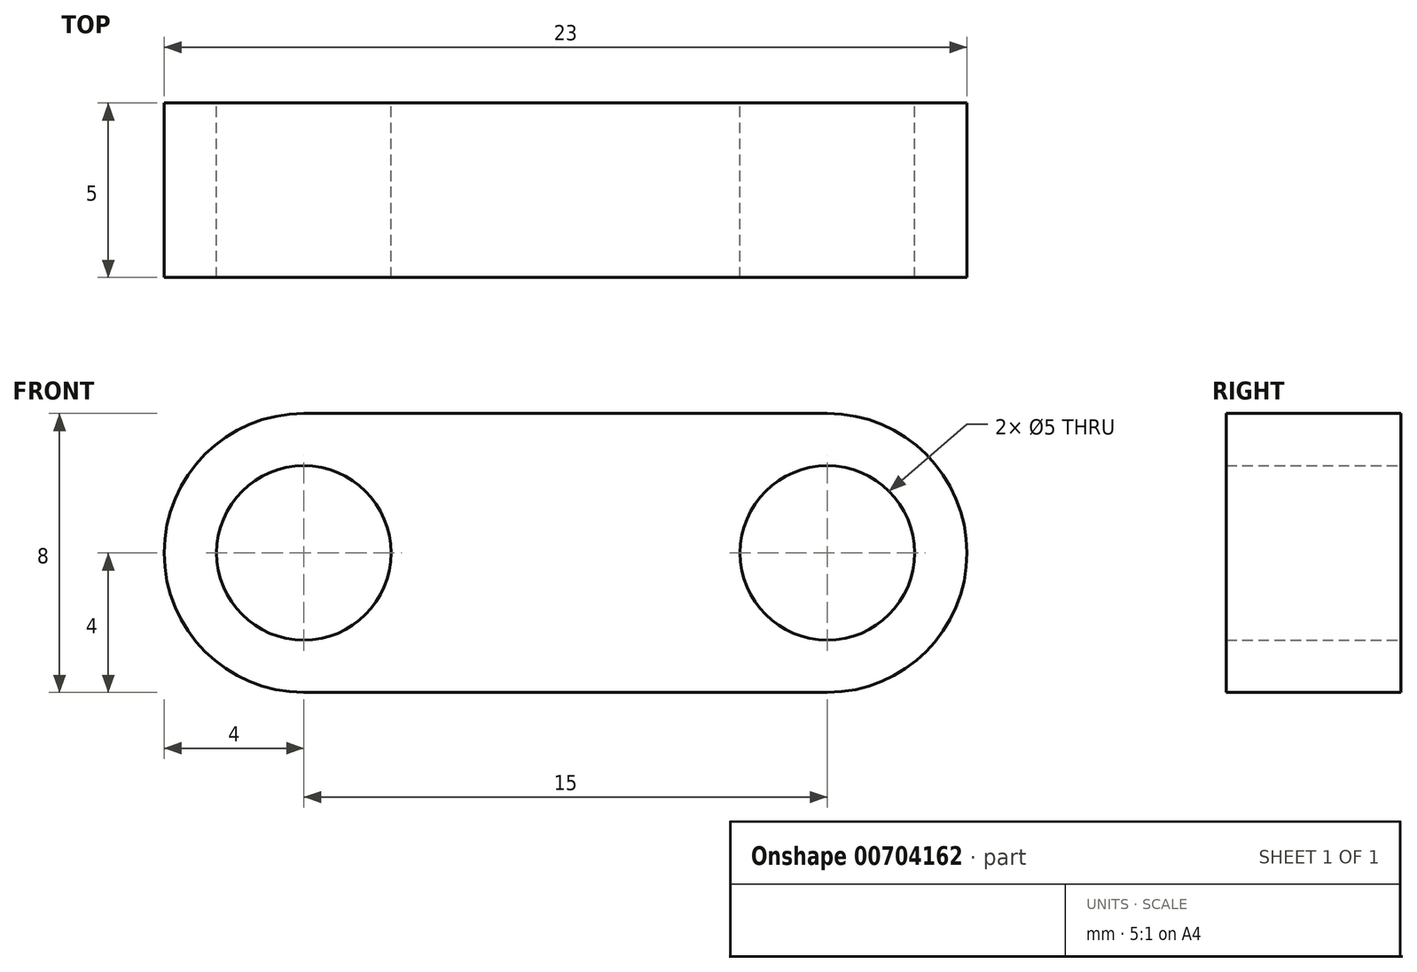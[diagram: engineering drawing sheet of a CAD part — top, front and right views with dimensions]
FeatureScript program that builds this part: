
annotation { "Feature Type Name" : "Feature", "Feature Type Description" : "" }
export const myFeature = defineFeature(function(context is Context, id is Id, definition is map)
    precondition{}
    {
        {
            var Q0;
            Q0=qCreatedBy(makeId("Front.planeOp"),FACE);
            var sketch = newSketch(context, id + "F0", { "sketchPlane" : qUnion([Q0])});
            skLineSegment(sketch, "E0.bottom", {"start": v(-7.5, 4) * mm, "end": v(0, 4) * mm});
            skLineSegment(sketch, "E0.top", {"start": v(-7.5, -4) * mm, "end": v(0, -4) * mm});
            skLineSegment(sketch, "E0.left", {"start": v(-7.5, 4) * mm, "end": v(-7.5, -4) * mm, "construction": true});
            skLineSegment(sketch, "E0.right", {"start": v(0, 4) * mm, "end": v(0, -4) * mm});
            skArc(sketch, "E1", {"start": v(-7.5, -4) * mm, "mid": v(-11.5, 0) * mm, "end": v(-7.5, 4) * mm});
            skCircle(sketch, "E2", {"center": v(-7.5, 0) * mm, "radius": 2.5 * mm});
            skLineSegment(sketch, "E3.MirrorCS", {"start": v(7.5, -4) * mm, "end": v(0, -4) * mm});
            skArc(sketch, "E4.MirrorCS", {"start": v(7.5, -4) * mm, "mid": v(11.5, 0) * mm, "end": v(7.5, 4) * mm});
            skCircle(sketch, "E5.MirrorC", {"center": v(7.5, 0) * mm, "radius": 2.5 * mm});
            skLineSegment(sketch, "E6.MirrorCS", {"start": v(7.5, 4) * mm, "end": v(0, 4) * mm});
            skSolve(sketch);
        }
        {
            var Q0;
            Q0=makeQuery(id+"F0.imprint","IMPRINT",FACE,{"disambiguationData":[TD([[makeQuery(id+"F0.imprint","IMPRINT",EDGE,{"derivedFrom":sQuery(id+"F0.wireOp",EDGE,"E0.bottom")}),-1.0]])]});
            var Q1;
            Q1=makeQuery(id+"F0.imprint","IMPRINT",FACE,{"disambiguationData":[TD([[makeQuery(id+"F0.imprint","IMPRINT",EDGE,{"derivedFrom":sQuery(id+"F0.wireOp",EDGE,"E0.right")}),1.0]])]});
            extrude(context, id + "F1", {"entities" : qUnion([Q0, Q1]), "depth" : 5 * mm, "offsetDistance" : 25 * mm});
        }
    });
